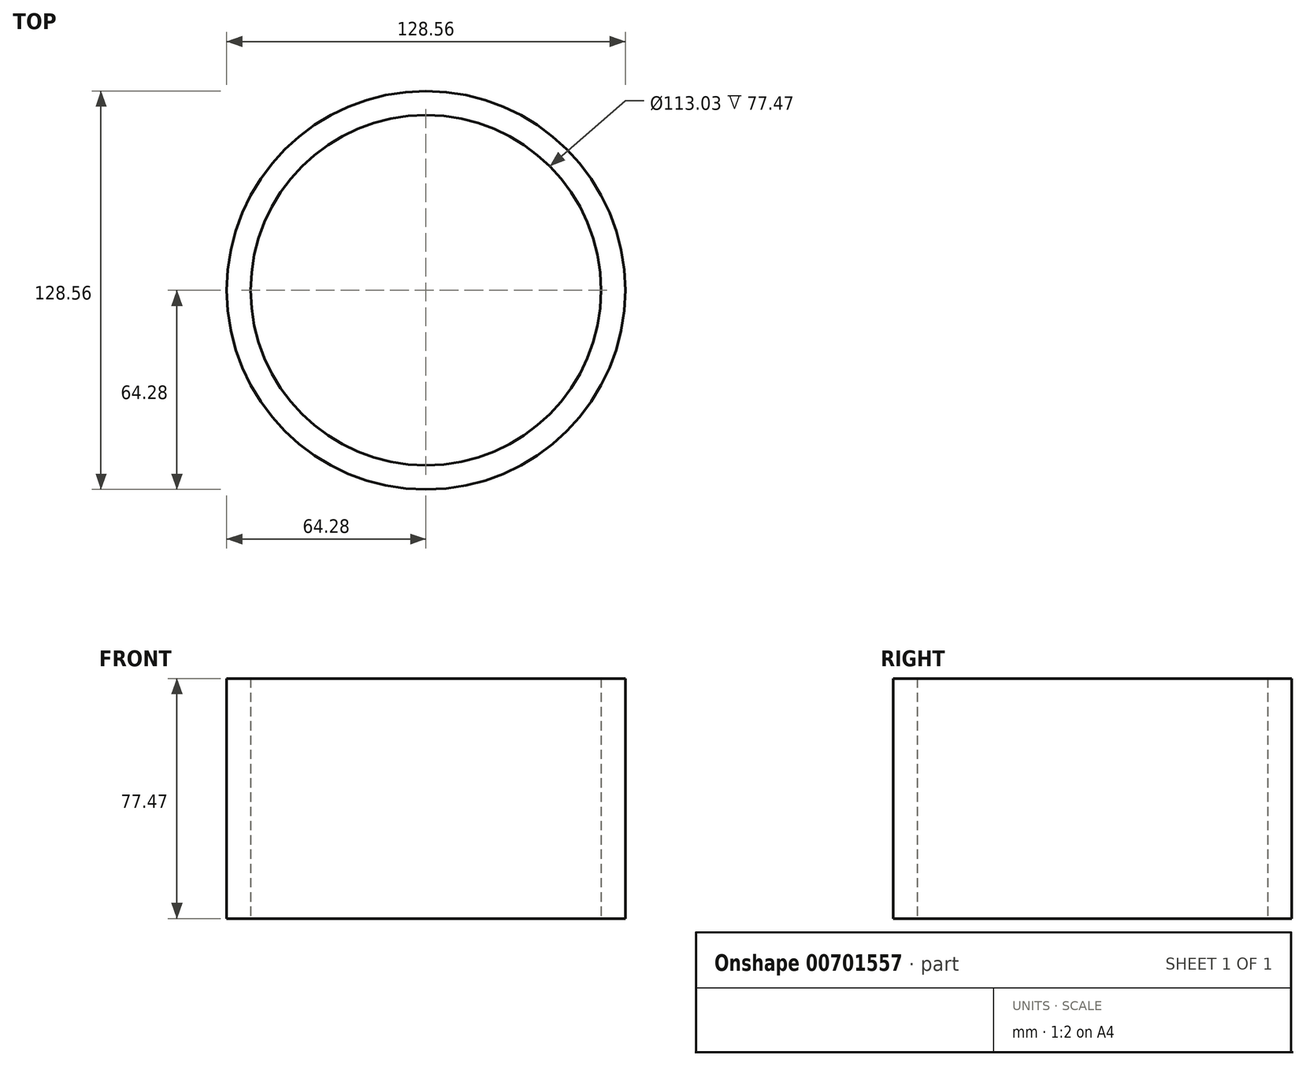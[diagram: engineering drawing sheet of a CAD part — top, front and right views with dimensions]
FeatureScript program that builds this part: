
annotation { "Feature Type Name" : "Feature", "Feature Type Description" : "" }
export const myFeature = defineFeature(function(context is Context, id is Id, definition is map)
    precondition{}
    {
        {
            var Q0;
            Q0=qCreatedBy(makeId("Top.planeOp"),FACE);
            var sketch = newSketch(context, id + "F0", { "sketchPlane" : qUnion([Q0])});
            skCircle(sketch, "E0", {"center": v(0, 0) * mm, "radius": 64.28 * mm});
            skCircle(sketch, "E1", {"center": v(0, 0) * mm, "radius": 56.52 * mm});
            skSolve(sketch);
        }
        {
            var Q0;
            Q0 = qSketchRegion(id + "F0", true);
            extrude(context, id + "F1", {"entities" : qUnion([Q0]), "depth" : 52.07 * mm, "offsetDistance" : 25.4 * mm});
        }
        {
            var Q0;
            Q0=qCreatedBy(makeId("Top.planeOp"),FACE);
            var sketch = newSketch(context, id + "F2", { "sketchPlane" : qUnion([Q0])});
            skCircle(sketch, "E2", {"center": v(0, 0) * mm, "radius": 59.67 * mm});
            skCircle(sketch, "E3", {"center": v(0, 0) * mm, "radius": 63.65 * mm});
            skSolve(sketch);
        }
        {
            var Q0;
            Q0 = qSketchRegion(id + "F2", true);
            extrude(context, id + "F3", {"entities" : qUnion([Q0]), "operationType" : NewBodyOperationType.ADD, "depth" : 28.2 * mm, "offsetDistance" : 25.4 * mm});
        }
        {
            var Q0;
            Q0=makeQuery(id+"F1.opExtrude","CAP_FACE",FACE,{"disambiguationData":[OSD([sQuery(id+"F0.wireOp",EDGE,"E0"),sQuery(id+"F0.wireOp",EDGE,"E1")])],"isStart":true});
            extrude(context, id + "F4", {"entities" : qUnion([Q0]), "operationType" : NewBodyOperationType.ADD, "depth" : 25.4 * mm, "offsetDistance" : 25.4 * mm});
        }
    });
